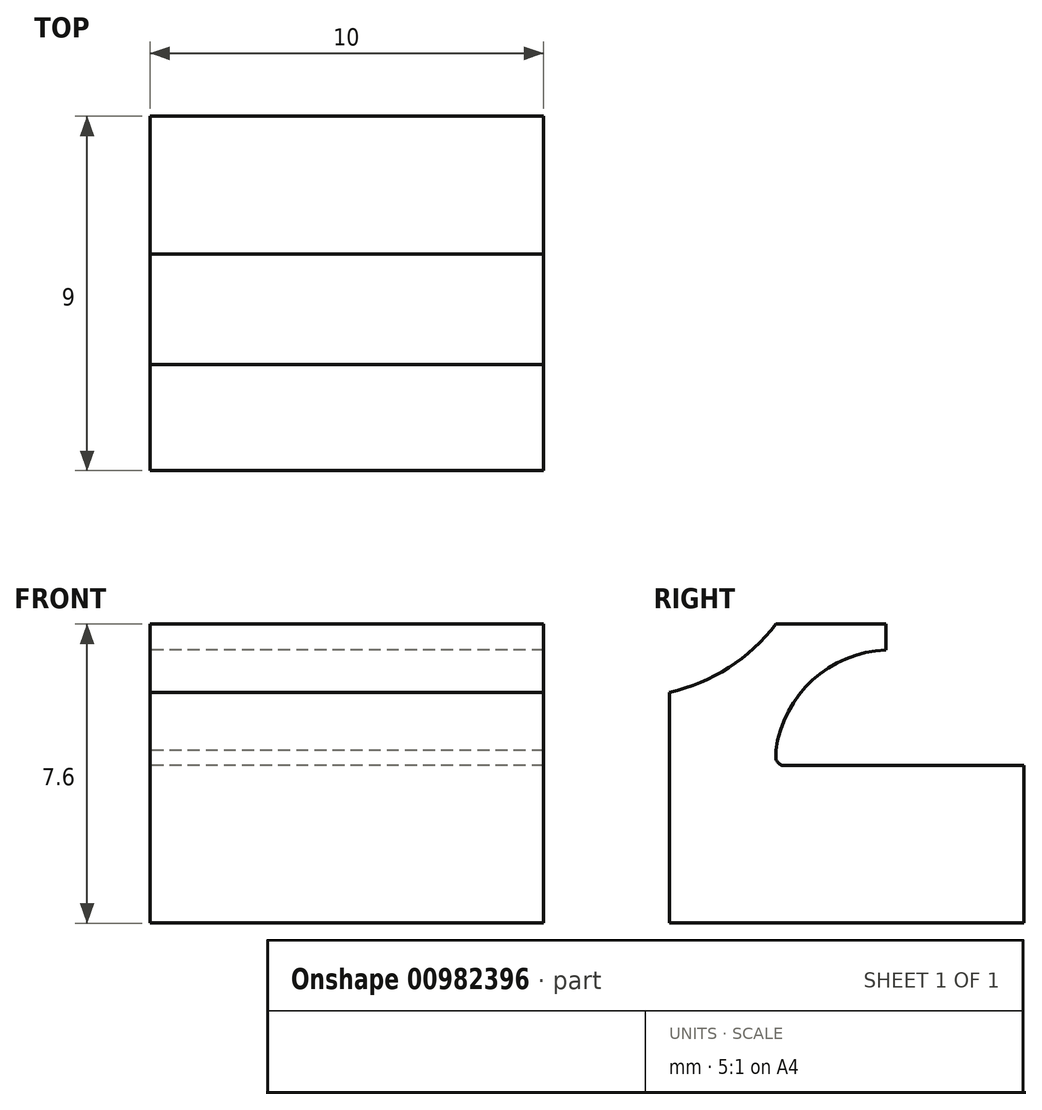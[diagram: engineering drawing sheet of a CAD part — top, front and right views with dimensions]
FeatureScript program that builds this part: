
annotation { "Feature Type Name" : "Feature", "Feature Type Description" : "" }
export const myFeature = defineFeature(function(context is Context, id is Id, definition is map)
    precondition{}
    {
        {
            var Q0;
            Q0=qCreatedBy(makeId("Right.planeOp"),FACE);
            var sketch = newSketch(context, id + "F0", { "sketchPlane" : qUnion([Q0])});
            skLineSegment(sketch, "E0.bottom", {"start": v(2.7, 2.31) * mm, "end": v(5.5, 2.31) * mm});
            skLineSegment(sketch, "E0.right", {"start": v(5.5, 2.31) * mm, "end": v(5.5, 1.65) * mm});
            skLineSegment(sketch, "E1", {"start": v(2.7, -1.07) * mm, "end": v(2.7, -0.9) * mm});
            skLineSegment(sketch, "E2.top", {"start": v(0, -5.29) * mm, "end": v(9, -5.29) * mm});
            skLineSegment(sketch, "E2.right", {"start": v(9, -1.29) * mm, "end": v(9, -5.29) * mm});
            skLineSegment(sketch, "E3", {"start": v(2.92, -1.29) * mm, "end": v(9, -1.29) * mm});
            skArc(sketch, "E4", {"start": v(0, 0.58) * mm, "mid": v(1.5, 1.2) * mm, "end": v(2.7, 2.31) * mm});
            skPoint(sketch, "E5.visualSharp", {"position": v(2.7, -1.29) * mm});
            skArc(sketch, "E5.filletArc", {"start": v(2.7, -1.07) * mm, "mid": v(2.76, -1.22) * mm, "end": v(2.92, -1.29) * mm});
            skArc(sketch, "E6", {"start": v(5.5, 1.65) * mm, "mid": v(3.63, 0.89) * mm, "end": v(2.7, -0.9) * mm});
            skLineSegment(sketch, "E7", {"start": v(0, 0.58) * mm, "end": v(0, -5.29) * mm});
            skLineSegment(sketch, "E8", {"start": v(2.7, -0.9) * mm, "end": v(2.7, 6.55) * mm, "construction": true});
            skSolve(sketch);
        }
        {
            var Q0;
            Q0 = qSketchRegion(id + "F0", true);
            extrude(context, id + "F1", {"entities" : qUnion([Q0]), "depth" : 10 * mm, "offsetDistance" : 25.4 * mm});
        }
    });
